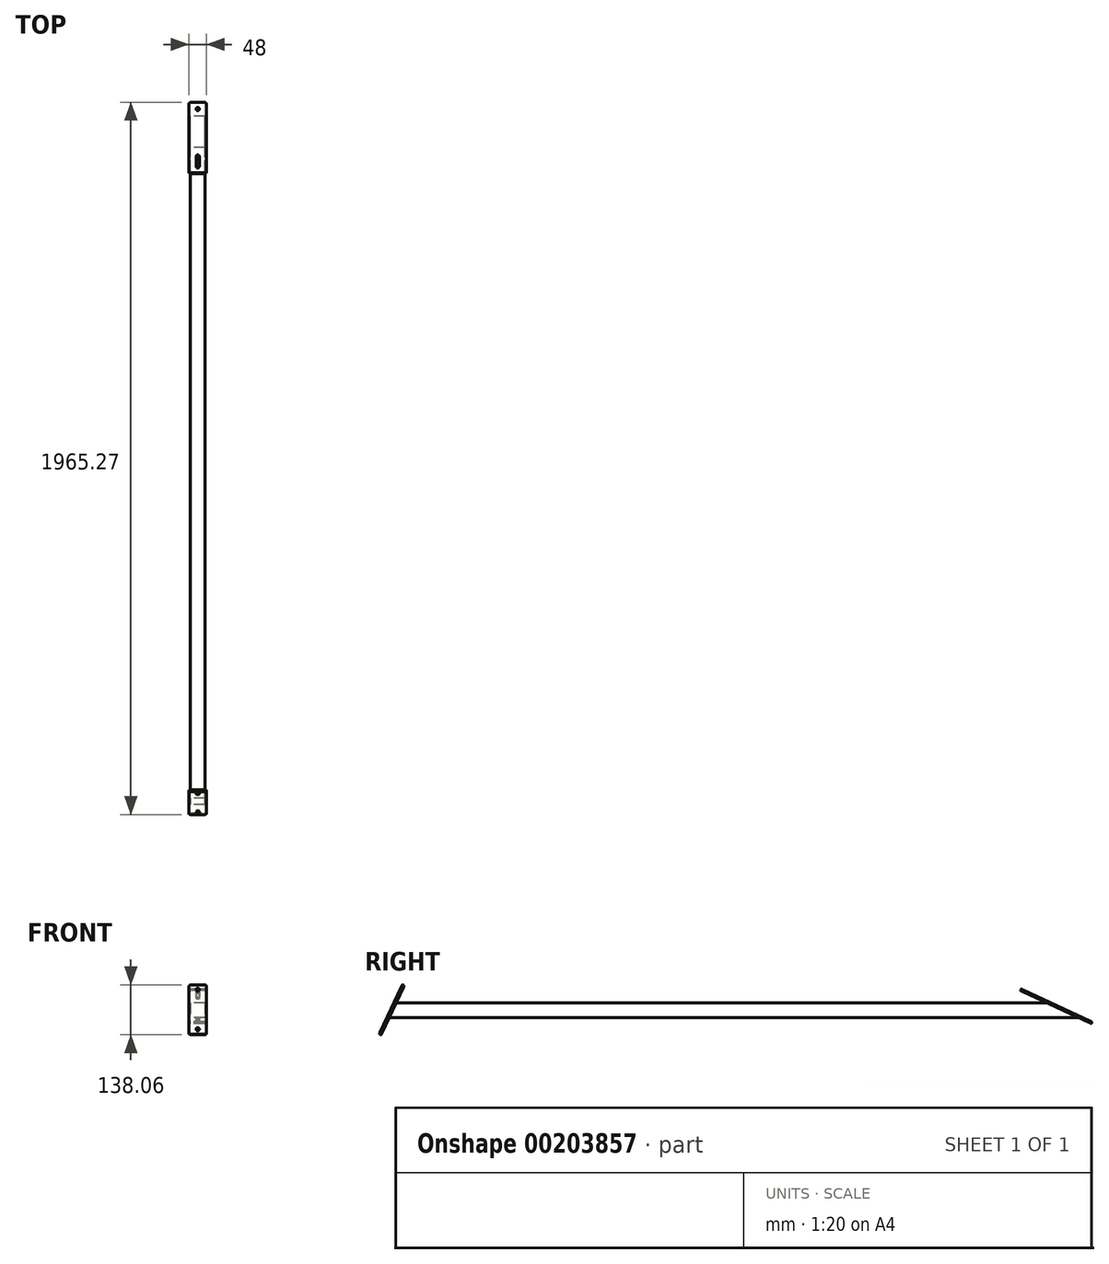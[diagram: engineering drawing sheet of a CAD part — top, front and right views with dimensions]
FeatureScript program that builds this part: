
annotation { "Feature Type Name" : "Feature", "Feature Type Description" : "" }
export const myFeature = defineFeature(function(context is Context, id is Id, definition is map)
    precondition{}
    {
        {
            var Q0;
            Q0=qCreatedBy(makeId("Front.planeOp"),FACE);
            var sketch = newSketch(context, id + "F0", { "sketchPlane" : qUnion([Q0])});
            skLineSegment(sketch, "E0.bottom", {"start": v(20, -20) * mm, "end": v(-20, -20) * mm});
            skLineSegment(sketch, "E0.top", {"start": v(20, 20) * mm, "end": v(-20, 20) * mm});
            skLineSegment(sketch, "E0.left", {"start": v(20, -20) * mm, "end": v(20, 20) * mm});
            skLineSegment(sketch, "E0.right", {"start": v(-20, -20) * mm, "end": v(-20, 20) * mm});
            skPoint(sketch, "E0.middle", {"position": v(0, 0) * mm});
            skSolve(sketch);
        }
        {
            var Q0;
            Q0 = qSketchRegion(id + "F0", true);
            extrude(context, id + "F1", {"entities" : qUnion([Q0]), "depth" : 1900 * mm});
        }
        {
            var Q0;
            Q0=makeQuery(id+"F1.opExtrude","SWEPT_FACE",FACE,{"disambiguationData":[OSD([sQuery(id+"F0.wireOp",EDGE,"E0.right")])]});
            var sketch = newSketch(context, id + "F2", { "sketchPlane" : qUnion([Q0])});
            skLineSegment(sketch, "E1", {"start": v(0, 20) * mm, "end": v(85.78, 20) * mm});
            skLineSegment(sketch, "E2", {"start": v(85.78, 20) * mm, "end": v(0, -20) * mm});
            skLineSegment(sketch, "E3", {"start": v(0, -20) * mm, "end": v(0, 20) * mm});
            skLineSegment(sketch, "E4", {"start": v(1900, 20) * mm, "end": v(1881.35, 20) * mm});
            skLineSegment(sketch, "E5", {"start": v(1881.35, 20) * mm, "end": v(1900, -20) * mm});
            skLineSegment(sketch, "E6", {"start": v(1900, -20) * mm, "end": v(1900, 20) * mm});
            skSolve(sketch);
        }
        {
            var Q0;
            Q0 = qSketchRegion(id + "F2", true);
            extrude(context, id + "F3", {"entities" : qUnion([Q0]), "operationType" : NewBodyOperationType.REMOVE, "endBound" : BoundingType.THROUGH_ALL, "oppositeDirection" : true, "depth" : 25 * mm});
        }
        {
            var Q0;
            Q0=makeQuery(id+"F3.boolean.opBoolean","COPY",FACE,{"derivedFrom":makeQuery(id+"F3.opExtrude","SWEPT_FACE",FACE,{"disambiguationData":[OSD([sQuery(id+"F2.wireOp",EDGE,"E2")])]})});
            var sketch = newSketch(context, id + "F4", { "sketchPlane" : qUnion([Q0])});
            skLineSegment(sketch, "E7", {"start": v(0, 8.45) * mm, "end": v(0, -86.2) * mm, "construction": true});
            skLineSegment(sketch, "E8.bottom", {"start": v(24, -166.2) * mm, "end": v(-24, -166.2) * mm});
            skLineSegment(sketch, "E8.top", {"start": v(24, 48.45) * mm, "end": v(-24, 48.45) * mm});
            skLineSegment(sketch, "E8.left", {"start": v(24, -166.2) * mm, "end": v(24, 48.45) * mm});
            skLineSegment(sketch, "E8.right", {"start": v(-24, -166.2) * mm, "end": v(-24, 48.45) * mm});
            skPoint(sketch, "E8.middle", {"position": v(0, -58.87) * mm});
            skSolve(sketch);
        }
        {
            var Q0;
            Q0 = qSketchRegion(id + "F4", true);
            extrude(context, id + "F5", {"entities" : qUnion([Q0]), "operationType" : NewBodyOperationType.ADD, "depth" : 5 * mm});
        }
        {
            var Q0;
            Q0=makeQuery(id+"F3.boolean.opBoolean","COPY",FACE,{"derivedFrom":makeQuery(id+"F3.opExtrude","SWEPT_FACE",FACE,{"disambiguationData":[OSD([sQuery(id+"F2.wireOp",EDGE,"E5")])]})});
            var sketch = newSketch(context, id + "F6", { "sketchPlane" : qUnion([Q0])});
            skLineSegment(sketch, "E9.bottom", {"start": v(-24, -874.03) * mm, "end": v(24, -874.03) * mm});
            skLineSegment(sketch, "E9.top", {"start": v(-24, -724.03) * mm, "end": v(24, -724.03) * mm});
            skLineSegment(sketch, "E9.left", {"start": v(-24, -874.03) * mm, "end": v(-24, -724.03) * mm});
            skLineSegment(sketch, "E9.right", {"start": v(24, -874.03) * mm, "end": v(24, -724.03) * mm});
            skPoint(sketch, "E9.middle", {"position": v(0, -799.03) * mm});
            skPoint(sketch, "E9.middle.positionSnap0", {"position": v(0, -776.97) * mm});
            skPoint(sketch, "E9.middle.positionSnap1", {"position": v(20, -799.03) * mm});
            skPoint(sketch, "E9.centerSnap0", {"position": v(0, -776.97) * mm});
            skPoint(sketch, "E9.centerSnap1", {"position": v(20, -799.03) * mm});
            skSolve(sketch);
        }
        {
            var Q0;
            Q0 = qSketchRegion(id + "F6", true);
            extrude(context, id + "F7", {"entities" : qUnion([Q0]), "operationType" : NewBodyOperationType.ADD, "depth" : 5 * mm});
        }
        {
            var Q0;
            Q0=makeQuery(id+"F7.opExtrude","CAP_FACE",FACE,{"disambiguationData":[OSD([sQuery(id+"F6.wireOp",EDGE,"E9.bottom"),sQuery(id+"F6.wireOp",EDGE,"E9.top"),sQuery(id+"F6.wireOp",EDGE,"E9.left"),sQuery(id+"F6.wireOp",EDGE,"E9.right")])],"isStart":false});
            var sketch = newSketch(context, id + "F8", { "sketchPlane" : qUnion([Q0])});
            skLineSegment(sketch, "E10", {"start": v(0, -874.03) * mm, "end": v(0, -724.03) * mm, "construction": true});
            skCircle(sketch, "E11", {"center": v(0, -859.03) * mm, "radius": 4.5 * mm});
            skLineSegment(sketch, "E12", {"start": v(-24, -799.03) * mm, "end": v(24, -799.03) * mm, "construction": true});
            skCircle(sketch, "E13.MirrorC", {"center": v(0, -739.03) * mm, "radius": 4.5 * mm});
            skSolve(sketch);
        }
        {
            var Q0;
            Q0 = qSketchRegion(id + "F8", true);
            extrude(context, id + "F9", {"entities" : qUnion([Q0]), "operationType" : NewBodyOperationType.REMOVE, "endBound" : BoundingType.UP_TO_NEXT, "oppositeDirection" : true, "depth" : 25 * mm});
        }
        {
            var Q0;
            Q0=makeQuery(id+"F5.opExtrude","CAP_FACE",FACE,{"disambiguationData":[OSD([sQuery(id+"F4.wireOp",EDGE,"E8.bottom"),sQuery(id+"F4.wireOp",EDGE,"E8.top"),sQuery(id+"F4.wireOp",EDGE,"E8.left"),sQuery(id+"F4.wireOp",EDGE,"E8.right")])],"isStart":false});
            var sketch = newSketch(context, id + "F10", { "sketchPlane" : qUnion([Q0])});
            skLineSegment(sketch, "E14", {"start": v(0, 48.45) * mm, "end": v(0, -166.2) * mm, "construction": true});
            skCircle(sketch, "E15", {"center": v(0, 28.45) * mm, "radius": 4.5 * mm});
            skCircle(sketch, "E16", {"center": v(0, -146.2) * mm, "radius": 4.5 * mm});
            skLineSegment(sketch, "E17.bottom", {"start": v(-4.5, -146.2) * mm, "end": v(4.5, -146.2) * mm});
            skLineSegment(sketch, "E17.top", {"start": v(-4.5, -116.2) * mm, "end": v(4.5, -116.2) * mm});
            skLineSegment(sketch, "E17.left", {"start": v(-4.5, -146.2) * mm, "end": v(-4.5, -116.2) * mm});
            skLineSegment(sketch, "E17.right", {"start": v(4.5, -146.2) * mm, "end": v(4.5, -116.2) * mm});
            skPoint(sketch, "E17.middle", {"position": v(0, -131.2) * mm});
            skArc(sketch, "E18", {"start": v(4.5, -116.2) * mm, "mid": v(0, -111.7) * mm, "end": v(-4.5, -116.2) * mm});
            skPoint(sketch, "E18.endSnap0", {"position": v(0, -116.2) * mm});
            skSolve(sketch);
        }
        {
            var Q0;
            Q0 = qSketchRegion(id + "F10", true);
            extrude(context, id + "F11", {"entities" : qUnion([Q0]), "operationType" : NewBodyOperationType.REMOVE, "endBound" : BoundingType.UP_TO_NEXT, "oppositeDirection" : true, "depth" : 25 * mm});
        }
        {
            var Q0;
            Q0=makeQuery(id+"F5.opExtrude","SWEPT_EDGE",EDGE,{"disambiguationData":[OSD([sQuery(id+"F4.wireOp",EDGE,"E8.top"),sQuery(id+"F4.wireOp",EDGE,"E8.right")])]});
            var Q1;
            Q1=makeQuery(id+"F5.opExtrude","SWEPT_EDGE",EDGE,{"disambiguationData":[OSD([sQuery(id+"F4.wireOp",EDGE,"E8.bottom"),sQuery(id+"F4.wireOp",EDGE,"E8.right")])]});
            var Q2;
            Q2=makeQuery(id+"F5.opExtrude","SWEPT_EDGE",EDGE,{"disambiguationData":[OSD([sQuery(id+"F4.wireOp",EDGE,"E8.top"),sQuery(id+"F4.wireOp",EDGE,"E8.left")])]});
            var Q3;
            Q3=makeQuery(id+"F5.opExtrude","SWEPT_EDGE",EDGE,{"disambiguationData":[OSD([sQuery(id+"F4.wireOp",EDGE,"E8.bottom"),sQuery(id+"F4.wireOp",EDGE,"E8.left")])]});
            var Q4;
            Q4=makeQuery(id+"F7.opExtrude","SWEPT_EDGE",EDGE,{"disambiguationData":[OSD([sQuery(id+"F6.wireOp",EDGE,"E9.bottom"),sQuery(id+"F6.wireOp",EDGE,"E9.left")])]});
            var Q5;
            Q5=makeQuery(id+"F7.opExtrude","SWEPT_EDGE",EDGE,{"disambiguationData":[OSD([sQuery(id+"F6.wireOp",EDGE,"E9.bottom"),sQuery(id+"F6.wireOp",EDGE,"E9.right")])]});
            var Q6;
            Q6=makeQuery(id+"F7.opExtrude","SWEPT_EDGE",EDGE,{"disambiguationData":[OSD([sQuery(id+"F6.wireOp",EDGE,"E9.top"),sQuery(id+"F6.wireOp",EDGE,"E9.right")])]});
            var Q7;
            Q7=makeQuery(id+"F7.opExtrude","SWEPT_EDGE",EDGE,{"disambiguationData":[OSD([sQuery(id+"F6.wireOp",EDGE,"E9.top"),sQuery(id+"F6.wireOp",EDGE,"E9.left")])]});
            fillet(context, id + "F12", {"entities" : qUnion([Q0, Q1, Q2, Q3, Q4, Q5, Q6, Q7]), "radius" : 5 * mm, "tangentPropagation" : true, "allowEdgeOverflow" : false});
        }
    });
